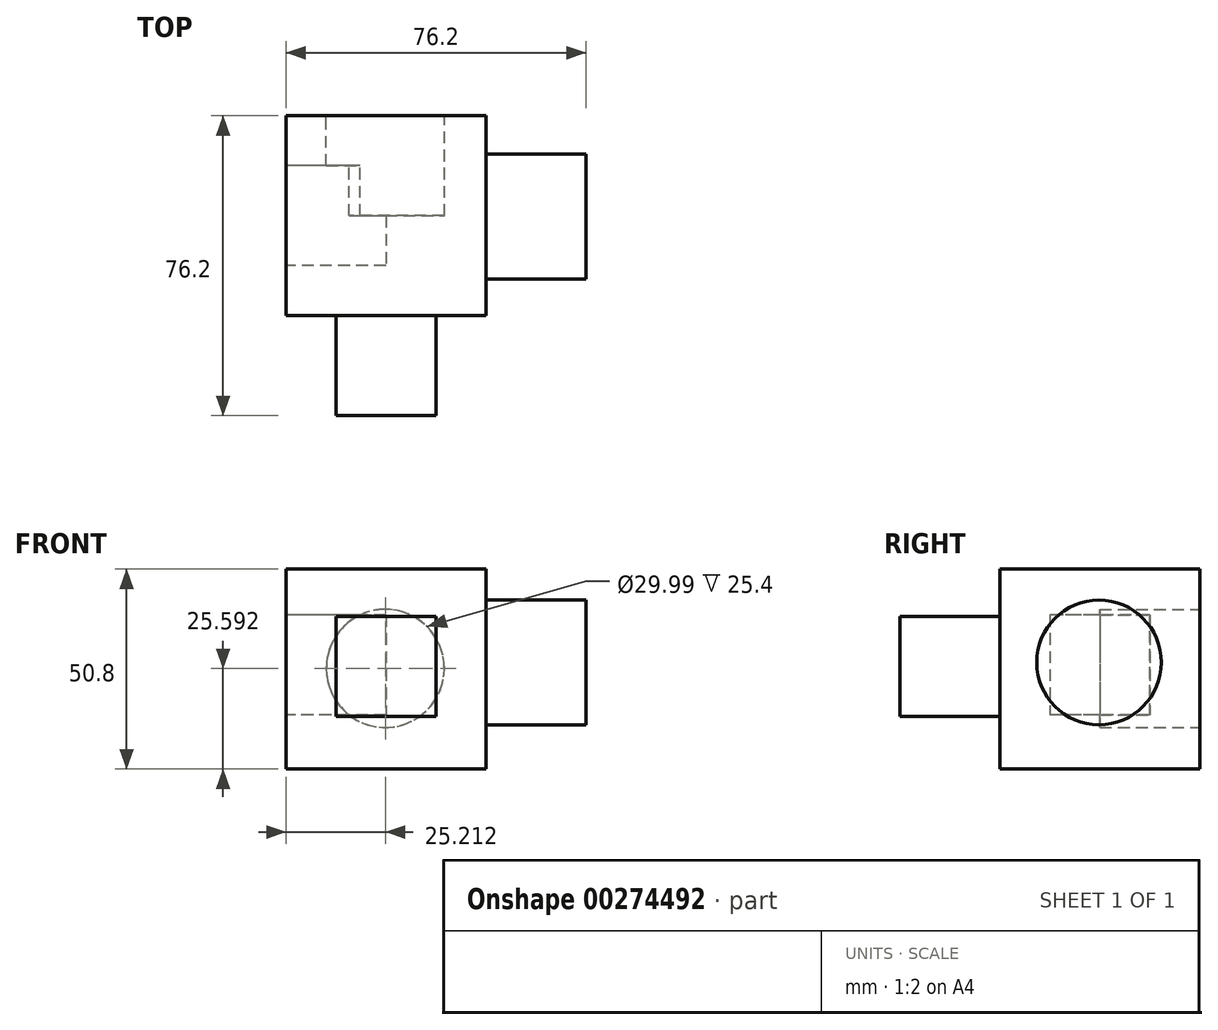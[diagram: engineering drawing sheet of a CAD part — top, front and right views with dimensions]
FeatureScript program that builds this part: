
annotation { "Feature Type Name" : "Feature", "Feature Type Description" : "" }
export const myFeature = defineFeature(function(context is Context, id is Id, definition is map)
    precondition{}
    {
        {
            var Q0;
            Q0=qCreatedBy(makeId("Front.planeOp"),FACE);
            var sketch = newSketch(context, id + "F0", { "sketchPlane" : qUnion([Q0])});
            skLineSegment(sketch, "E0.bottom", {"start": v(-64.74, 61.68) * mm, "end": v(-13.94, 61.68) * mm});
            skLineSegment(sketch, "E0.top", {"start": v(-64.74, 10.88) * mm, "end": v(-13.94, 10.88) * mm});
            skLineSegment(sketch, "E0.left", {"start": v(-64.74, 61.68) * mm, "end": v(-64.74, 10.88) * mm});
            skLineSegment(sketch, "E0.right", {"start": v(-13.94, 61.68) * mm, "end": v(-13.94, 10.88) * mm});
            skSolve(sketch);
        }
        {
            var Q0;
            Q0 = qSketchRegion(id + "F0", true);
            extrude(context, id + "F1", {"entities" : qUnion([Q0]), "depth" : 50.8 * mm});
        }
        {
            var Q0;
            Q0=makeQuery(id+"F1.opExtrude","CAP_FACE",FACE,{"disambiguationData":[OSD([sQuery(id+"F0.wireOp",EDGE,"E0.bottom"),sQuery(id+"F0.wireOp",EDGE,"E0.top"),sQuery(id+"F0.wireOp",EDGE,"E0.left"),sQuery(id+"F0.wireOp",EDGE,"E0.right")])],"isStart":false});
            var sketch = newSketch(context, id + "F2", { "sketchPlane" : qUnion([Q0])});
            skLineSegment(sketch, "E1.bottom", {"start": v(-52.04, 49.65) * mm, "end": v(-26.64, 49.65) * mm});
            skLineSegment(sketch, "E1.top", {"start": v(-52.04, 24.25) * mm, "end": v(-26.64, 24.25) * mm});
            skLineSegment(sketch, "E1.left", {"start": v(-52.04, 49.65) * mm, "end": v(-52.04, 24.25) * mm});
            skLineSegment(sketch, "E1.right", {"start": v(-26.64, 49.65) * mm, "end": v(-26.64, 24.25) * mm});
            skSolve(sketch);
        }
        {
            var Q0;
            Q0 = qSketchRegion(id + "F2", true);
            extrude(context, id + "F3", {"entities" : qUnion([Q0]), "operationType" : NewBodyOperationType.ADD, "depth" : 25.4 * mm});
        }
        {
            var Q0;
            Q0=makeQuery(id+"F1.opExtrude","SWEPT_FACE",FACE,{"disambiguationData":[OSD([sQuery(id+"F0.wireOp",EDGE,"E0.left")])]});
            var sketch = newSketch(context, id + "F4", { "sketchPlane" : qUnion([Q0])});
            skLineSegment(sketch, "E2.bottom", {"start": v(12.7, 50.03) * mm, "end": v(38.1, 50.03) * mm});
            skLineSegment(sketch, "E2.top", {"start": v(12.7, 24.63) * mm, "end": v(38.1, 24.63) * mm});
            skLineSegment(sketch, "E2.left", {"start": v(12.7, 50.03) * mm, "end": v(12.7, 24.63) * mm});
            skLineSegment(sketch, "E2.right", {"start": v(38.1, 50.03) * mm, "end": v(38.1, 24.63) * mm});
            skSolve(sketch);
        }
        {
            var Q0;
            Q0 = qSketchRegion(id + "F4", true);
            extrude(context, id + "F5", {"entities" : qUnion([Q0]), "operationType" : NewBodyOperationType.REMOVE, "oppositeDirection" : true, "depth" : 25.4 * mm});
        }
        {
            var Q0;
            Q0=makeQuery(id+"F1.opExtrude","SWEPT_FACE",FACE,{"disambiguationData":[OSD([sQuery(id+"F0.wireOp",EDGE,"E0.right")])]});
            var sketch = newSketch(context, id + "F6", { "sketchPlane" : qUnion([Q0])});
            skCircle(sketch, "E3", {"center": v(-25.59, 38) * mm, "radius": 15.84 * mm});
            skSolve(sketch);
        }
        {
            var Q0;
            Q0 = qSketchRegion(id + "F6", true);
            extrude(context, id + "F7", {"entities" : qUnion([Q0]), "operationType" : NewBodyOperationType.ADD, "depth" : 25.4 * mm});
        }
        {
            var Q0;
            Q0=makeQuery(id+"F1.opExtrude","CAP_FACE",FACE,{"disambiguationData":[OSD([sQuery(id+"F0.wireOp",EDGE,"E0.bottom"),sQuery(id+"F0.wireOp",EDGE,"E0.top"),sQuery(id+"F0.wireOp",EDGE,"E0.left"),sQuery(id+"F0.wireOp",EDGE,"E0.right")])],"isStart":true});
            var sketch = newSketch(context, id + "F8", { "sketchPlane" : qUnion([Q0])});
            skCircle(sketch, "E4", {"center": v(39.53, 36.47) * mm, "radius": 15 * mm});
            skSolve(sketch);
        }
        {
            var Q0;
            Q0=makeQuery(id+"F8.imprint","IMPRINT",FACE,{"disambiguationData":[TD([[makeQuery(id+"F8.imprint","IMPRINT",EDGE,{"derivedFrom":sQuery(id+"F8.wireOp",EDGE,"E4")}),1.0]])]});
            extrude(context, id + "F9", {"entities" : qUnion([Q0]), "operationType" : NewBodyOperationType.REMOVE, "oppositeDirection" : true, "depth" : 25.4 * mm});
        }
    });
